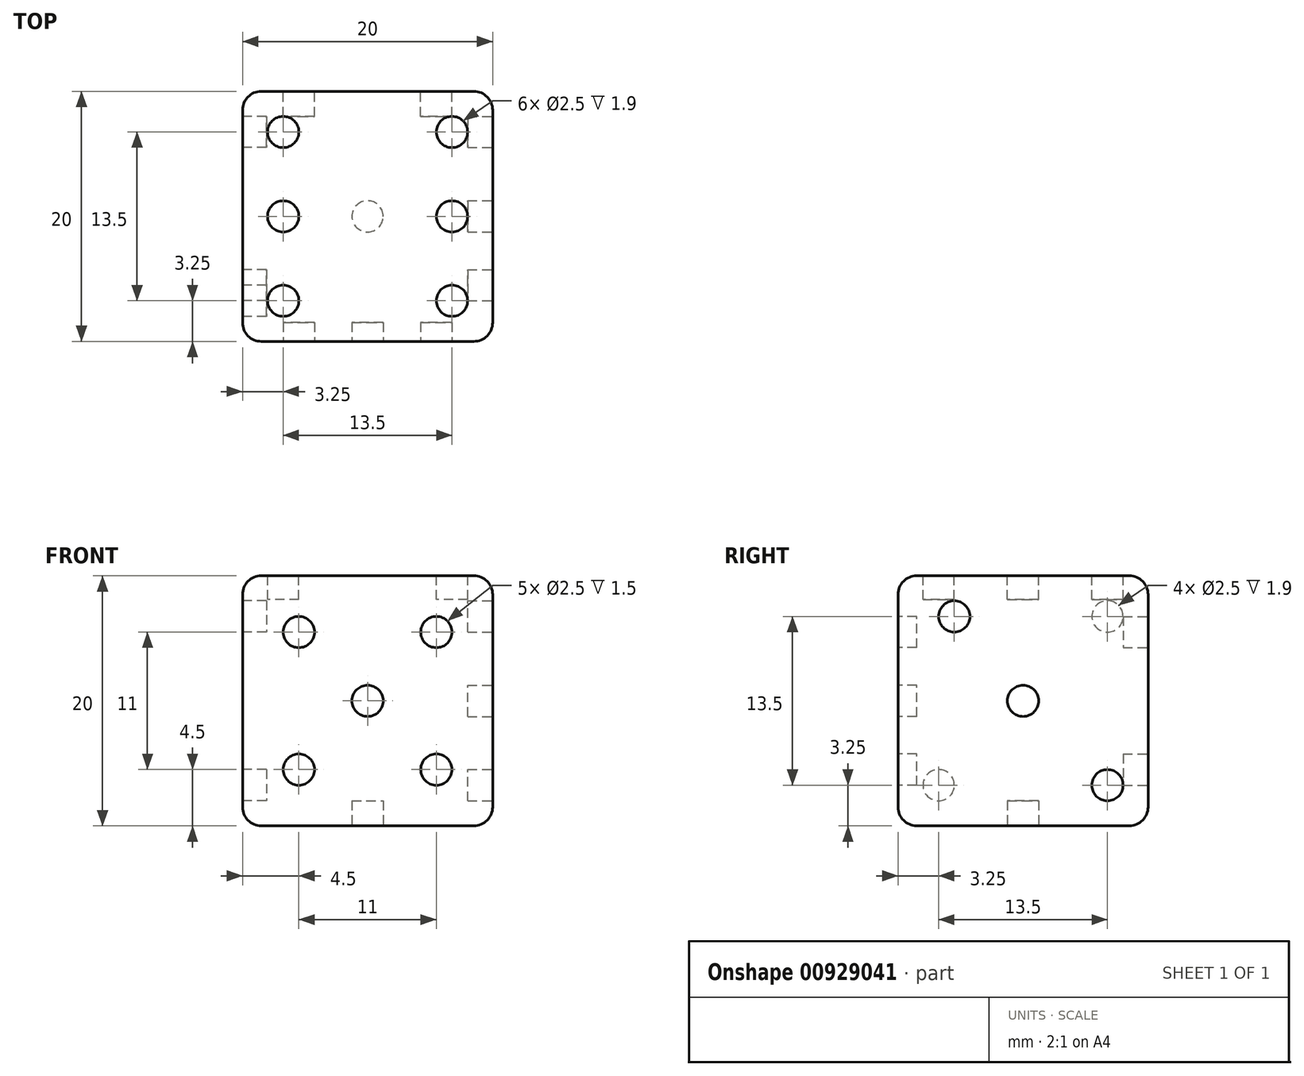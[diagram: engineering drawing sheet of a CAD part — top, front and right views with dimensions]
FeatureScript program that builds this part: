
annotation { "Feature Type Name" : "Feature", "Feature Type Description" : "" }
export const myFeature = defineFeature(function(context is Context, id is Id, definition is map)
    precondition{}
    {
        {
            var Q0;
            Q0=qCreatedBy(makeId("Top.planeOp"),FACE);
            var sketch = newSketch(context, id + "F0", { "sketchPlane" : qUnion([Q0])});
            skLineSegment(sketch, "E0.bottom", {"start": v(-10, -10) * mm, "end": v(10, -10) * mm});
            skLineSegment(sketch, "E0.top", {"start": v(-10, 10) * mm, "end": v(10, 10) * mm});
            skLineSegment(sketch, "E0.left", {"start": v(-10, -10) * mm, "end": v(-10, 10) * mm});
            skLineSegment(sketch, "E0.right", {"start": v(10, -10) * mm, "end": v(10, 10) * mm});
            skPoint(sketch, "E0.middle", {"position": v(0, 0) * mm});
            skSolve(sketch);
        }
        {
            var Q0;
            Q0=makeQuery(id+"F0.imprint","IMPRINT",FACE,{"disambiguationData":[TD([[makeQuery(id+"F0.imprint","IMPRINT",EDGE,{"derivedFrom":sQuery(id+"F0.wireOp",EDGE,"E0.bottom")}),1.0]])]});
            extrude(context, id + "F1", {"entities" : qUnion([Q0]), "depth" : 20 * mm, "offsetDistance" : 25 * mm});
        }
        {
            var Q0;
            Q0=makeQuery(id+"F1.opExtrude","SWEPT_FACE",FACE,{"disambiguationData":[OSD([sQuery(id+"F0.wireOp",EDGE,"E0.top")])]});
            var Q1;
            Q1=makeQuery(id+"F1.opExtrude","SWEPT_FACE",FACE,{"disambiguationData":[OSD([sQuery(id+"F0.wireOp",EDGE,"E0.bottom")])]});
            var Q2;
            Q2=makeQuery(id+"F1.opExtrude","CAP_FACE",FACE,{"disambiguationData":[OSD([sQuery(id+"F0.wireOp",EDGE,"E0.bottom"),sQuery(id+"F0.wireOp",EDGE,"E0.top"),sQuery(id+"F0.wireOp",EDGE,"E0.left"),sQuery(id+"F0.wireOp",EDGE,"E0.right")])],"isStart":false});
            var Q3;
            Q3=makeQuery(id+"F1.opExtrude","SWEPT_FACE",FACE,{"disambiguationData":[OSD([sQuery(id+"F0.wireOp",EDGE,"E0.right")])]});
            var Q4;
            Q4=makeQuery(id+"F1.opExtrude","CAP_EDGE",EDGE,{"disambiguationData":[OSD([sQuery(id+"F0.wireOp",EDGE,"E0.left")])],"isStart":true});
            fillet(context, id + "F2", {"entities" : qUnion([Q0, Q1, Q2, Q3, Q4]), "radius" : 1.5 * mm, "tangentPropagation" : true, "allowEdgeOverflow" : false});
        }
        {
            var Q0;
            Q0=makeQuery(id+"F1.opExtrude","SWEPT_FACE",FACE,{"disambiguationData":[OSD([sQuery(id+"F0.wireOp",EDGE,"E0.right")])]});
            var sketch = newSketch(context, id + "F3", { "sketchPlane" : qUnion([Q0])});
            skCircle(sketch, "E1", {"center": v(0, 10) * mm, "radius": 1.25 * mm});
            skPoint(sketch, "E1.centerSnap0", {"position": v(10, 10) * mm});
            skPoint(sketch, "E1.centerSnap1", {"position": v(0, 0) * mm});
            skCircle(sketch, "E2", {"center": v(-5.5, 16.75) * mm, "radius": 1.25 * mm});
            skCircle(sketch, "E3", {"center": v(6.75, 3.25) * mm, "radius": 1.25 * mm});
            skSolve(sketch);
        }
        {
            var Q0;
            Q0=makeQuery(id+"F3.imprint","IMPRINT",FACE,{"disambiguationData":[TD([[makeQuery(id+"F3.imprint","IMPRINT",EDGE,{"derivedFrom":sQuery(id+"F3.wireOp",EDGE,"E2")}),1.0]])]});
            var Q1;
            Q1=makeQuery(id+"F3.imprint","IMPRINT",FACE,{"disambiguationData":[TD([[makeQuery(id+"F3.imprint","IMPRINT",EDGE,{"derivedFrom":sQuery(id+"F3.wireOp",EDGE,"E1")}),1.0]])]});
            var Q2;
            Q2=makeQuery(id+"F3.imprint","IMPRINT",FACE,{"disambiguationData":[TD([[makeQuery(id+"F3.imprint","IMPRINT",EDGE,{"derivedFrom":sQuery(id+"F3.wireOp",EDGE,"E3")}),1.0]])]});
            var Q3;
            Q3=sQuery(id+"F3.wireOp",EDGE,"E2");
            var Q4;
            Q4=sQuery(id+"F3.wireOp",EDGE,"E1");
            var Q5;
            Q5=sQuery(id+"F3.wireOp",EDGE,"E3");
            extrude(context, id + "F4", {"entities" : qUnion([Q0, Q1, Q2]), "operationType" : NewBodyOperationType.REMOVE, "surfaceEntities" : qUnion([Q3, Q4, Q5]), "oppositeDirection" : true, "depth" : 2 * mm, "offsetDistance" : 25 * mm});
        }
        {
            var Q0;
            Q0=makeQuery(id+"F1.opExtrude","SWEPT_FACE",FACE,{"disambiguationData":[OSD([sQuery(id+"F0.wireOp",EDGE,"E0.bottom")])]});
            var sketch = newSketch(context, id + "F5", { "sketchPlane" : qUnion([Q0])});
            skCircle(sketch, "E4", {"center": v(0, 10) * mm, "radius": 1.25 * mm});
            skPoint(sketch, "E4.centerSnap0", {"position": v(10, 10) * mm});
            skCircle(sketch, "E5", {"center": v(-5.5, 15.5) * mm, "radius": 1.25 * mm});
            skCircle(sketch, "E6", {"center": v(5.5, 4.5) * mm, "radius": 1.25 * mm});
            skCircle(sketch, "E7", {"center": v(5.5, 15.5) * mm, "radius": 1.25 * mm});
            skCircle(sketch, "E8", {"center": v(-5.5, 4.5) * mm, "radius": 1.25 * mm});
            skSolve(sketch);
        }
        {
            var Q0;
            Q0=makeQuery(id+"F5.imprint","IMPRINT",FACE,{"disambiguationData":[TD([[makeQuery(id+"F5.imprint","IMPRINT",EDGE,{"derivedFrom":sQuery(id+"F5.wireOp",EDGE,"E8")}),1.0]])]});
            var Q1;
            Q1=makeQuery(id+"F5.imprint","IMPRINT",FACE,{"disambiguationData":[TD([[makeQuery(id+"F5.imprint","IMPRINT",EDGE,{"derivedFrom":sQuery(id+"F5.wireOp",EDGE,"E7")}),1.0]])]});
            var Q2;
            Q2=makeQuery(id+"F5.imprint","IMPRINT",FACE,{"disambiguationData":[TD([[makeQuery(id+"F5.imprint","IMPRINT",EDGE,{"derivedFrom":sQuery(id+"F5.wireOp",EDGE,"E5")}),1.0]])]});
            var Q3;
            Q3=makeQuery(id+"F5.imprint","IMPRINT",FACE,{"disambiguationData":[TD([[makeQuery(id+"F5.imprint","IMPRINT",EDGE,{"derivedFrom":sQuery(id+"F5.wireOp",EDGE,"E4")}),1.0]])]});
            var Q4;
            Q4=makeQuery(id+"F5.imprint","IMPRINT",FACE,{"disambiguationData":[TD([[makeQuery(id+"F5.imprint","IMPRINT",EDGE,{"derivedFrom":sQuery(id+"F5.wireOp",EDGE,"E6")}),1.0]])]});
            extrude(context, id + "F6", {"entities" : qUnion([Q0, Q1, Q2, Q3, Q4]), "operationType" : NewBodyOperationType.REMOVE, "oppositeDirection" : true, "depth" : 1.5 * mm, "offsetDistance" : 25 * mm});
        }
        {
            var Q0;
            Q0=makeQuery(id+"F1.opExtrude","SWEPT_FACE",FACE,{"disambiguationData":[OSD([sQuery(id+"F0.wireOp",EDGE,"E0.top")])]});
            var sketch = newSketch(context, id + "F7", { "sketchPlane" : qUnion([Q0])});
            skCircle(sketch, "E9", {"center": v(-5.5, 15.5) * mm, "radius": 1.25 * mm});
            skCircle(sketch, "E10", {"center": v(5.5, 4.5) * mm, "radius": 1.25 * mm});
            skSolve(sketch);
        }
        {
            var Q0;
            Q0 = qSketchRegion(id + "F7", true);
            extrude(context, id + "F8", {"entities" : qUnion([Q0]), "operationType" : NewBodyOperationType.REMOVE, "oppositeDirection" : true, "depth" : 2 * mm, "offsetDistance" : 25 * mm});
        }
        {
            var Q0;
            Q0=makeQuery(id+"F1.opExtrude","SWEPT_FACE",FACE,{"disambiguationData":[OSD([sQuery(id+"F0.wireOp",EDGE,"E0.left")])]});
            var sketch = newSketch(context, id + "F9", { "sketchPlane" : qUnion([Q0])});
            skCircle(sketch, "E11", {"center": v(-6.75, 3.25) * mm, "radius": 1.25 * mm});
            skCircle(sketch, "E12", {"center": v(5.5, 16.75) * mm, "radius": 1.25 * mm});
            skCircle(sketch, "E13", {"center": v(6.75, 3.25) * mm, "radius": 1.25 * mm});
            skCircle(sketch, "E14", {"center": v(-6.75, 16.75) * mm, "radius": 1.25 * mm});
            skSolve(sketch);
        }
        {
            var Q0;
            Q0 = qSketchRegion(id + "F9", true);
            extrude(context, id + "F10", {"entities" : qUnion([Q0]), "operationType" : NewBodyOperationType.REMOVE, "oppositeDirection" : true, "depth" : 1.9 * mm, "offsetDistance" : 25 * mm});
        }
        {
            var Q0;
            Q0=makeQuery(id+"F1.opExtrude","CAP_FACE",FACE,{"disambiguationData":[OSD([sQuery(id+"F0.wireOp",EDGE,"E0.bottom"),sQuery(id+"F0.wireOp",EDGE,"E0.top"),sQuery(id+"F0.wireOp",EDGE,"E0.left"),sQuery(id+"F0.wireOp",EDGE,"E0.right")])],"isStart":false});
            var sketch = newSketch(context, id + "F11", { "sketchPlane" : qUnion([Q0])});
            skCircle(sketch, "E15", {"center": v(-6.75, 6.75) * mm, "radius": 1.25 * mm});
            skCircle(sketch, "E16", {"center": v(-6.75, -6.75) * mm, "radius": 1.25 * mm});
            skCircle(sketch, "E17", {"center": v(-6.75, 0) * mm, "radius": 1.25 * mm});
            skCircle(sketch, "E18", {"center": v(6.75, 6.75) * mm, "radius": 1.25 * mm});
            skCircle(sketch, "E19", {"center": v(6.75, 0) * mm, "radius": 1.25 * mm});
            skCircle(sketch, "E20", {"center": v(6.75, -6.75) * mm, "radius": 1.25 * mm});
            skSolve(sketch);
        }
        {
            var Q0;
            Q0 = qSketchRegion(id + "F11", true);
            extrude(context, id + "F12", {"entities" : qUnion([Q0]), "operationType" : NewBodyOperationType.REMOVE, "oppositeDirection" : true, "depth" : 1.9 * mm, "offsetDistance" : 25 * mm});
        }
        {
            var Q0;
            Q0=makeQuery(id+"F1.opExtrude","CAP_FACE",FACE,{"disambiguationData":[OSD([sQuery(id+"F0.wireOp",EDGE,"E0.bottom"),sQuery(id+"F0.wireOp",EDGE,"E0.top"),sQuery(id+"F0.wireOp",EDGE,"E0.left"),sQuery(id+"F0.wireOp",EDGE,"E0.right")])],"isStart":true});
            var sketch = newSketch(context, id + "F13", { "sketchPlane" : qUnion([Q0])});
            skCircle(sketch, "E21", {"center": v(0, 0) * mm, "radius": 1.25 * mm});
            skSolve(sketch);
        }
        {
            var Q0;
            Q0 = qSketchRegion(id + "F13", true);
            extrude(context, id + "F14", {"entities" : qUnion([Q0]), "operationType" : NewBodyOperationType.REMOVE, "oppositeDirection" : true, "depth" : 2 * mm, "offsetDistance" : 25 * mm});
        }
    });
